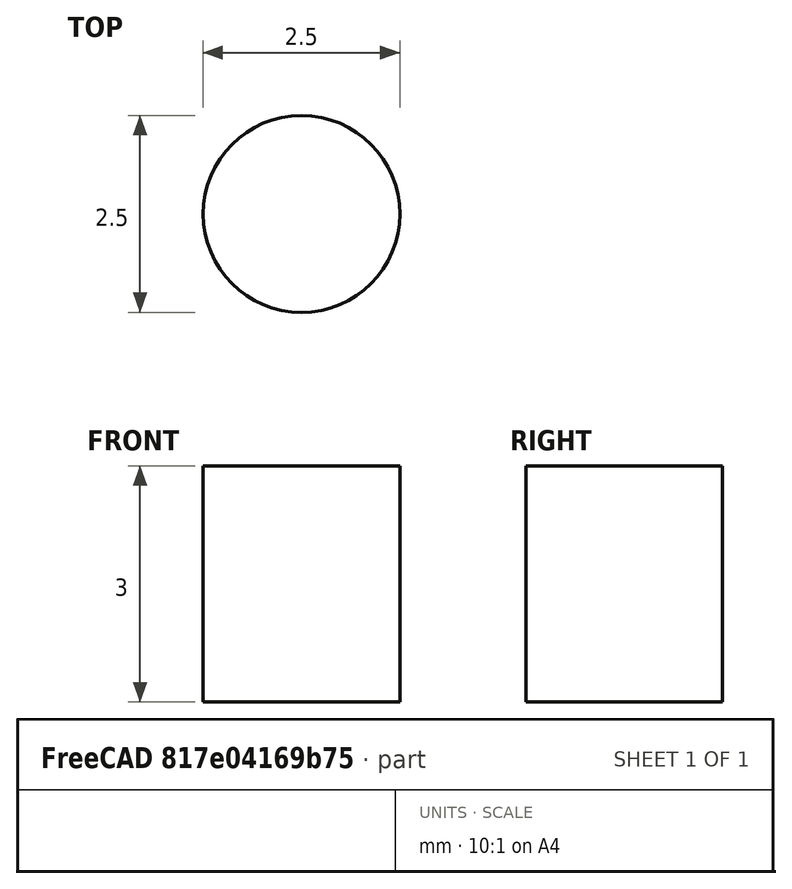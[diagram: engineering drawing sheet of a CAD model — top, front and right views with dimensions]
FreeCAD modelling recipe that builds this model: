
FCSTD DOCUMENT  (FreeCAD 0.19R)
Label: screw_shc_M3x12
License: All rights reserved
LicenseURL: http://en.wikipedia.org/wiki/All_rights_reserved
objects: Part::Feature×1, PartDesign::CoordinateSystem×1, Sketcher::SketchObject×1, PartDesign::Pad×1, PartDesign::Body×1
note: 6 computed .brp shape members not serialized (recipe doc carries the construction recipe); baked Part::Feature solids carry a one-line shape summary decoded from their .brp

FEATURE [Part::Feature] _1292A114_18_8_Stainless_Steel_Socket_Head_Screw  label="screw_shc_M3x12"
  shape: bbox 5.5 x 5.5 x 15.03 mm, 125 faces, 0 solids (baked)
FEATURE [PartDesign::CoordinateSystem] Local_CS  label="LCS_screw_shc_M3x12"
  AttacherType = Attacher::AttachEngine3D
  MapMode = 11
  Placement = pos=(0,0,-12) rot=(-0.707107,0.707107,0;3.14159rad)
FEATURE [Sketcher::SketchObject] Sketch
  FullyConstrained = true
  MapMode = 5
  Support = -> [XY_Plane]
  sketch-geometry (1):
    g0: Circle CenterX=0 CenterY=0 CenterZ=0 NormalX=0 NormalY=0 NormalZ=1 AngleXU=0 Radius=1.25
  constraints (2):
    c: Coincident(g0,g-1)
    c: Diameter(g0) = 2.5
FEATURE [PartDesign::Pad] Pad
  Direction = (1,1,1)
  Length = 3
  Length2 = 100
  Profile = -> Sketch
  Refine = true
  Type = 0
FEATURE [PartDesign::Body] Body
  Group = -> [Local_CS,Sketch,Pad]
  Origin = -> Origin
  Tip = -> Pad
